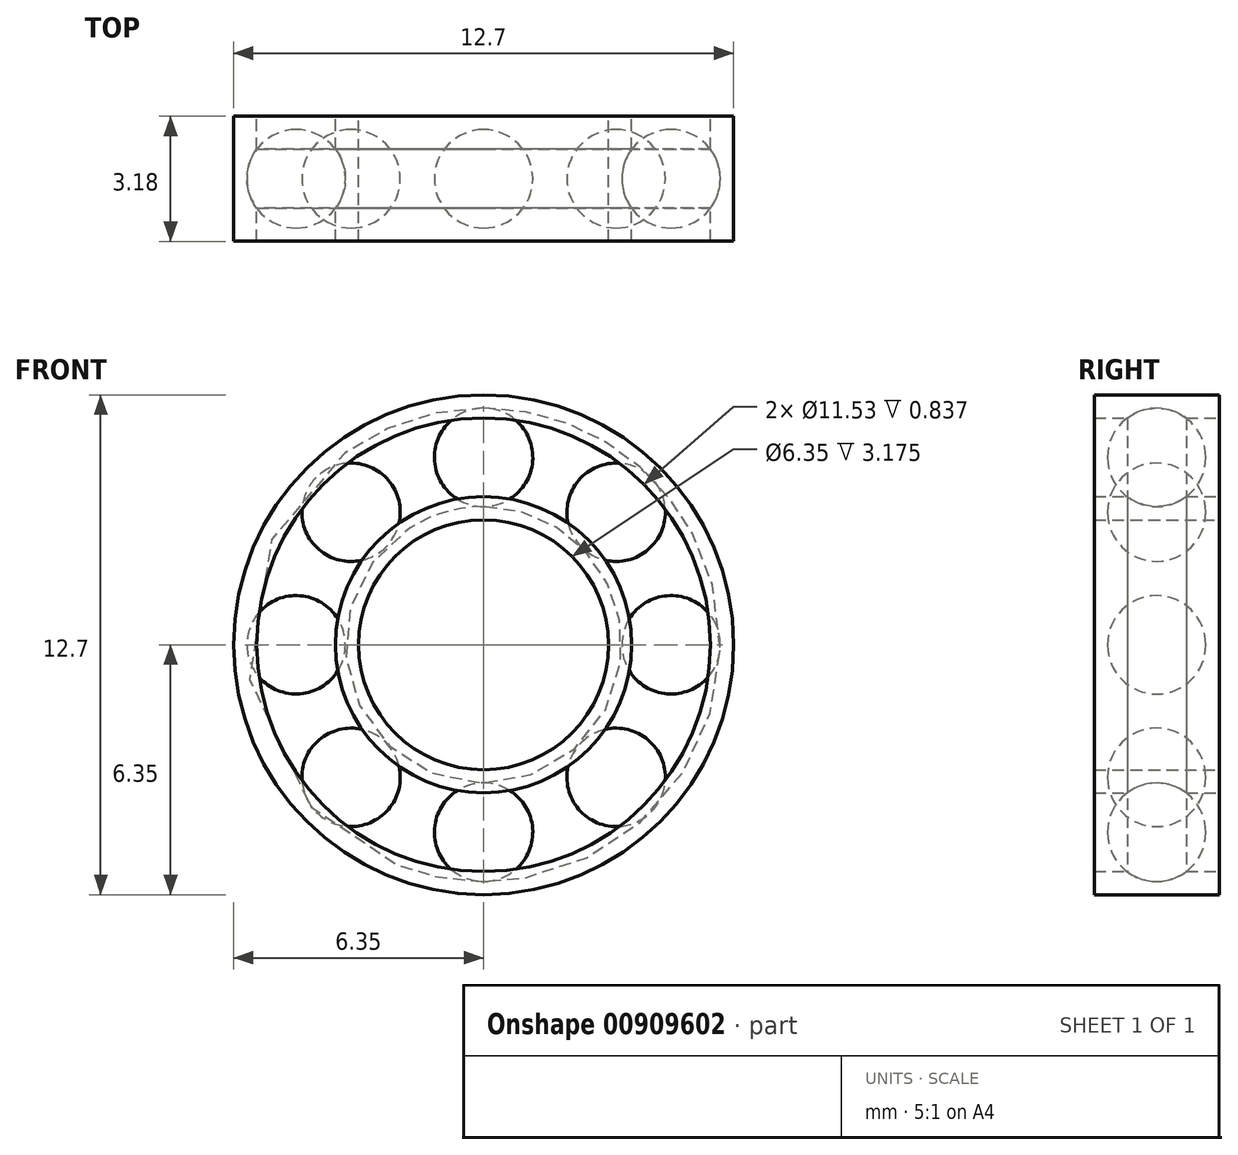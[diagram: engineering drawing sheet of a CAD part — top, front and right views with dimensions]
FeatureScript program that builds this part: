
annotation { "Feature Type Name" : "Feature", "Feature Type Description" : "" }
export const myFeature = defineFeature(function(context is Context, id is Id, definition is map)
    precondition{}
    {
        {
            var Q0;
            Q0=qCreatedBy(makeId("Top.planeOp"),FACE);
            var sketch = newSketch(context, id + "F0", { "sketchPlane" : qUnion([Q0])});
            skLineSegment(sketch, "E0.bottom", {"start": v(-6.35, 1.59) * mm, "end": v(-3.17, 1.59) * mm});
            skLineSegment(sketch, "E0.top", {"start": v(-6.35, -1.59) * mm, "end": v(-3.17, -1.59) * mm});
            skLineSegment(sketch, "E0.left", {"start": v(-6.35, 1.59) * mm, "end": v(-6.35, -1.59) * mm});
            skLineSegment(sketch, "E0.right", {"start": v(-3.18, 1.59) * mm, "end": v(-3.18, -1.59) * mm});
            skLineSegment(sketch, "E1", {"start": v(-4.76, 1.59) * mm, "end": v(-4.76, -1.59) * mm});
            skLineSegment(sketch, "E2", {"start": v(-6.35, 0) * mm, "end": v(-3.18, 0) * mm, "construction": true});
            skCircle(sketch, "E3", {"center": v(-4.76, 0) * mm, "radius": 1.25 * mm});
            skLineSegment(sketch, "E4", {"start": v(-5.76, 1.59) * mm, "end": v(-5.76, -1.59) * mm});
            skLineSegment(sketch, "E5", {"start": v(-3.76, 1.59) * mm, "end": v(-3.76, -1.59) * mm});
            skLineSegment(sketch, "E6", {"start": v(0, 1.59) * mm, "end": v(0, -1.59) * mm, "construction": true});
            skSolve(sketch);
        }
        {
            var Q0;
            {var subQ4=sQuery(id+"F0.wireOp",EDGE,"E0.right");Q0=makeQuery(id+"F0.imprint","IMPRINT",FACE,{"disambiguationData":[TD([[makeQuery(id+"F0.imprint","IMPRINT",EDGE,{"derivedFrom":subQ4}),-1.0]])]});}
            var Q1;
            {var subQ4=sQuery(id+"F0.wireOp",EDGE,"E0.left");Q1=makeQuery(id+"F0.imprint","IMPRINT",FACE,{"disambiguationData":[TD([[makeQuery(id+"F0.imprint","IMPRINT",EDGE,{"derivedFrom":subQ4}),1.0]])]});}
            var Q2;
            Q2=sQuery(id+"F0.wireOp",EDGE,"E6");
            revolve(context, id + "F1", {"surfaceOperationType" : NewSurfaceOperationType.NEW, "entities" : qUnion([Q0, Q1]), "axis" : qUnion([Q2]), "revolveType" : RevolveType.FULL});
        }
        {
            var Q0;
            {var subQ0=sQuery(id+"F0.wireOp",EDGE,"E4");var subQ1=sQuery(id+"F0.wireOp",EDGE,"E3");var subQ2=makeQuery(id+"F0.imprint","INTERSECT",VERTEX,{"disambiguationData":[OD(0.0)],"derivedFrom":[subQ1,subQ0]});Q0=makeQuery(id+"F0.imprint","IMPRINT",FACE,{"disambiguationData":[TD([[makeQuery(id+"F0.imprint","IMPRINT",EDGE,{"disambiguationData":[TD([[subQ2,-1.0]])],"derivedFrom":subQ1}),1.0]])]});}
            var Q1;
            {var subQ0=sQuery(id+"F0.wireOp",EDGE,"E3");var subQ1=sQuery(id+"F0.wireOp",EDGE,"E1");var subQ2=makeQuery(id+"F0.imprint","INTERSECT",VERTEX,{"disambiguationData":[OD(0.0)],"derivedFrom":[subQ1,subQ0]});Q1=makeQuery(id+"F0.imprint","IMPRINT",FACE,{"disambiguationData":[TD([[makeQuery(id+"F0.imprint","IMPRINT",EDGE,{"disambiguationData":[TD([[subQ2,-1.0]])],"derivedFrom":subQ1}),-1.0]])]});}
            var Q2;
            Q2=sQuery(id+"F0.wireOp",EDGE,"E1");
            revolve(context, id + "F2", {"surfaceOperationType" : NewSurfaceOperationType.NEW, "entities" : qUnion([Q0, Q1]), "axis" : qUnion([Q2]), "revolveType" : RevolveType.FULL});
        }
        {
            var Q0;
            Q0=makeQuery(id+"F2.opRevolve","SWEPT_BODY",BODY,{"disambiguationData":[OSD([sQuery(id+"F0.wireOp",EDGE,"E1"),sQuery(id+"F0.wireOp",EDGE,"E3")])]});
            var Q1;
            Q1=sQuery(id+"F0.wireOp",EDGE,"E6");
            circularPattern(context, id + "F3", {"entities" : qUnion([Q0]), "axis" : qUnion([Q1]), "angle" : 360 * degree, "instanceCount" : 8, "equalSpace" : true});
        }
    });
